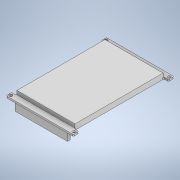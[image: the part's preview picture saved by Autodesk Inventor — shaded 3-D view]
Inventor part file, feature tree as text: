
AUTODESK INVENTOR PART (.ipt)
format: ipt  version: 2020 (Build 240168000, 168)  size: 217,600 bytes
history: native  units: mm
features: extrude x4, sketch x4, other x1
ambient origin geometry x8: Origin, YZ Plane, XZ Plane, XY Plane, X Axis, Y Axis, Z Axis, Center Point
bodies: Solid1 (feature_tree)
feature tree (9):
  extrude  "Vetronite"  Depth=97.0mm
  extrude  "Display"  Depth=5.2mm
  extrude  "Pin"  Depth=1.0mm
  extrude  "Componenti"  Depth=2.0mm
  other  "ScreenCables"
  sketch  "Sketch1"  dims[d0=56.0mm d1=97.0mm]
  sketch  "Sketch2"  dims[d2=4.5mm d3=5.2mm]
  sketch  "Sketch3"  dims[d8=1.7mm d9=0.0mm d10=1.0mm]
  sketch  "Sketch4"  dims[d11=1.0mm d12=2.0mm d13=2.6mm d14=3.0mm d15=56.0mm d16=85.0mm d17=56.0mm d18=3.6mm d19=0.0mm d20=50.6mm d21=2.5mm d22=1.5mm d23=8.5mm d24=0.0mm d25=16.0mm d26=14.0mm d27=12.0mm d28=12.0mm d29=12.0mm d30=12.0mm d31=30.0mm d32=16.0mm d33=15.0mm d34=5.0mm d35=28.0mm d36=6.0mm d37=2.0mm d38=57.0mm d40=13.0mm d41=2.5mm d42=0.0mm d43=13.962634mm]
